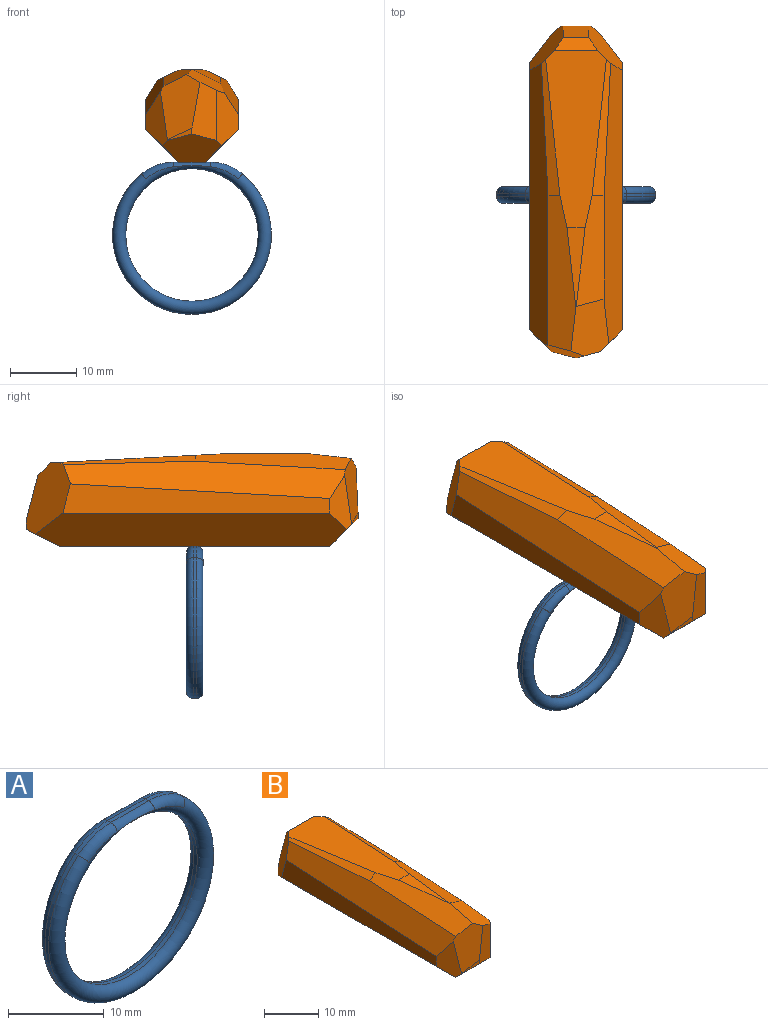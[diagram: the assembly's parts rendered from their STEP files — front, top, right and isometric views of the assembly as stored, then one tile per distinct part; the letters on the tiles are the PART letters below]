
ASSEMBLY  parts=2 mates=1
PART A: 13 faces, bbox 26x2.5x26 mm
  f0: plane 5.57x0.5mm, normal (0,0,1), area 2.8mm2, adj f3,f4,f8,f12
  f1: cylinder r=10mm len=20mm, axis (0,1,0), area 31.4mm2, adj f5,f9
  f2: cylinder r=12mm len=24mm, axis (0,1,0), area 29.4mm2, adj f3,f4,f5,f9
  f3: cylinder r=7.62mm len=4.85mm, axis (0,1,0), area 2.6mm2, adj f0,f2,f7,f10
  f4: cylinder r=7.62mm len=4.85mm, axis (0,1,0), area 2.6mm2, adj f0,f2,f6,f11
  f5: torus R=11mm, axis (0,-1,0), area 187.9mm2, adj f1,f2,f6,f7,f8
  f6: torus R=6.62mm, axis (0,-1,0), area 7.1mm2, adj f4,f5,f8
  f7: torus R=6.62mm, axis (0,-1,0), area 7.1mm2, adj f3,f5,f8
  f8: cylinder r=1mm len=5.57mm, axis (1,0,0), area 6.2mm2, adj f0,f5,f6,f7
  f9: torus R=11mm, axis (0,-1,0), area 187.9mm2, adj f1,f2,f10,f11,f12
  f10: torus R=6.62mm, axis (0,-1,0), area 7.1mm2, adj f3,f9,f12
  f11: torus R=6.62mm, axis (0,-1,0), area 7.1mm2, adj f4,f9,f12
  f12: cylinder r=1mm len=5.57mm, axis (-1,0,0), area 6.2mm2, adj f0,f9,f10,f11
PART B: 26 faces, bbox 14x50.2x14 mm
  f0: plane 40.84x4mm, normal (0,0,-1), area 163.4mm2, adj f8,f12,f13,f16
  f1: plane 40.37x4.42mm, normal (1,0,0), area 132.9mm2, adj f6,f11,f12,f14
  f2: plane 12.11x2.75mm, normal (0,0,1), area 16.9mm2, adj f5,f20,f23,f25
  f3: plane 4.5x1.3mm, normal (0,1,0), area 5.4mm2, adj f9,f13,f14,f15
  f4: plane 20.54x2.8mm, normal (0.45,0,0.89), area 28.2mm2, adj f5,f11,f14,f23
  f5: plane 16.79x4.19mm, normal (0.45,-0.05,0.89), area 57.2mm2, adj f2,f4,f11,f23,f25
  f6: plane 8.37x3.28mm, normal (0.71,-0.71,0), area 27.7mm2, adj f1,f8,f10,f11,f12,f25
  f7: plane 6.53x1.88mm, normal (0,0.71,0.71), area 13.8mm2, adj f9,f14,f15,f23
  f8: plane 9x4.25mm, normal (0,-0.71,-0.71), area 37.2mm2, adj f0,f6,f10,f12,f16,f18,f19
  f9: plane 6.88x3.84mm, normal (0,0.97,0.25), area 27.3mm2, adj f3,f7,f14,f15
  f10: plane 8.8x3.72mm, normal (0.25,-0.97,0), area 26.1mm2, adj f6,f8,f18,f24,f25
  f11: plane 42.33x5.62mm, normal (0.85,-0.03,0.53), area 193.7mm2, adj f1,f4,f5,f6,f14,f25
  f12: plane 46.98x5mm, normal (0.71,0,-0.71), area 309.4mm2, adj f0,f1,f6,f8,f13,f14
  f13: plane 7.64x5.08mm, normal (0,0.45,-0.89), area 33.5mm2, adj f0,f3,f12,f14,f15,f16
  f14: plane 10.85x6.71mm, normal (0.71,0.68,0.18), area 64.8mm2, adj f1,f3,f4,f7,f9,f11,f12,f13
  f15: plane 10.85x6.71mm, normal (-0.71,0.68,0.18), area 64.8mm2, adj f3,f7,f9,f13,f16,f17,f21,f22
  f16: plane 46.98x5mm, normal (-0.71,0,-0.71), area 309.4mm2, adj f0,f8,f13,f15,f19,f22
  f17: plane 42.58x5.62mm, normal (-0.85,-0.03,0.53), area 198.5mm2, adj f15,f19,f20,f21,f22,f24
  f18: plane 3.72x1.88mm, normal (-0.25,-0.97,0), area 1.9mm2, adj f8,f10,f19,f24
  f19: plane 8.21x3.28mm, normal (-0.71,-0.71,0), area 22.3mm2, adj f8,f16,f17,f18,f22,f24
  f20: plane 23.53x4.21mm, normal (-0.45,-0.05,0.89), area 87mm2, adj f2,f17,f21,f23,f24,f25
  f21: plane 20.54x2.8mm, normal (-0.45,0,0.89), area 28.2mm2, adj f15,f17,f20,f23
  f22: plane 40.37x4.42mm, normal (-1,0,0), area 132.9mm2, adj f15,f16,f17,f19
  f23: plane 26.8x9.17mm, normal (0,0.05,1), area 173.8mm2, adj f2,f4,f5,f7,f14,f15,f20,f21
  f24: plane 9.9x5.98mm, normal (-0.29,-0.95,0.09), area 42.5mm2, adj f10,f17,f18,f19,f20,f25
  f25: plane 8.56x5.72mm, normal (0.46,-0.15,0.87), area 43.2mm2, adj f2,f5,f6,f10,f11,f20,f24
PLACE A t=(26.64,12.17,-4.13)mm
PLACE B t=(26.64,10.42,13.87)mm
MATE fastened B.f0 <-> A.f0  axis (0,0,-1) through (26.64,10.92,6.87)mm
